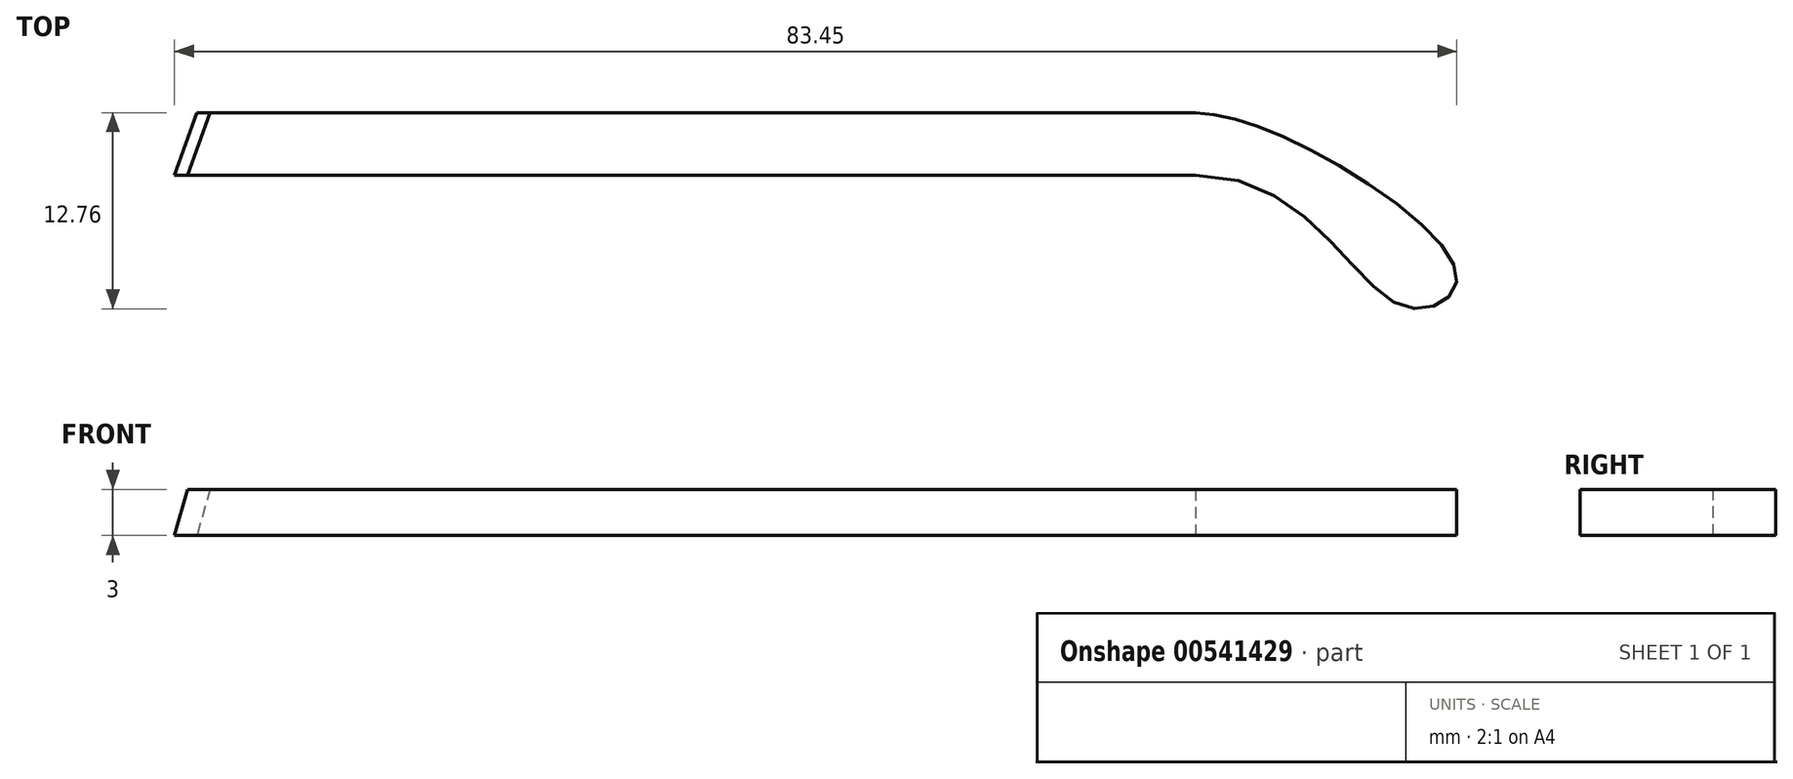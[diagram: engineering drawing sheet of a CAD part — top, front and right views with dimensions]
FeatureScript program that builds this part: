
annotation { "Feature Type Name" : "Feature", "Feature Type Description" : "" }
export const myFeature = defineFeature(function(context is Context, id is Id, definition is map)
    precondition{}
    {
        {
            var Q0;
            Q0=qCreatedBy(makeId("Top.planeOp"),FACE);
            var sketch = newSketch(context, id + "F0", { "sketchPlane" : qUnion([Q0])});
            skLineSegment(sketch, "E0", {"start": v(-34.31, 0) * mm, "end": v(30.69, 0) * mm});
            skFitSpline(sketch, "E1", {"points": [v(30.69, 0) * mm, v(44.1, -8.51) * mm, v(47.67, -6.87) * mm, v(39.2, 1.07) * mm, v(30.69, 4.06) * mm], "startDerivative": vector(69.74, 0) * mm, "endDerivative": vector(-26.04, 0.82) * mm});
            skLineSegment(sketch, "E2", {"start": v(30.69, 4.06) * mm, "end": v(-34.31, 4.06) * mm});
            skLineSegment(sketch, "E3", {"start": v(-34.31, 4.06) * mm, "end": v(-34.31, 0) * mm});
            skLineSegment(sketch, "E4", {"start": v(-34.31, 0) * mm, "end": v(-35.77, 0) * mm});
            skLineSegment(sketch, "E5", {"start": v(-35.77, 0) * mm, "end": v(-34.31, 4.06) * mm});
            skSolve(sketch);
        }
        {
            var Q0;
            Q0 = qSketchRegion(id + "F0", true);
            var Q1;
            Q1=makeQuery(id+"F0.imprint","IMPRINT",FACE,{"disambiguationData":[TD([[makeQuery(id+"F0.imprint","IMPRINT",EDGE,{"derivedFrom":sQuery(id+"F0.wireOp",EDGE,"E0")}),1.0]])]});
            extrude(context, id + "F1", {"entities" : qUnion([Q0, Q1]), "depth" : 3 * mm, "offsetDistance" : 25 * mm});
        }
        {
            var Q0;
            Q0=makeQuery(id+"F1.opExtrude","CAP_EDGE",EDGE,{"disambiguationData":[OSD([sQuery(id+"F0.wireOp",EDGE,"E5")])],"isStart":false});
            chamfer(context, id + "F2", {"entities" : qUnion([Q0]), "chamferType" : ChamferType.OFFSET_ANGLE, "width" : 3 * mm, "oppositeDirection" : false, "angle" : 15 * degree, "tangentPropagation" : true});
        }
    });
